FCSTD DOCUMENT  (FreeCAD 0.21R33771 (Git))
Label: Assemblage
License: All rights reserved
LicenseURL: http://en.wikipedia.org/wiki/All_rights_reserved
objects: App::DocumentObjectGroup×3, App::Link×2, PartDesign::CoordinateSystem×1, App::FeaturePython×1, App::Part×1
note: 1 computed .brp shape members not serialized (recipe doc carries the construction recipe); baked Part::Feature solids carry a one-line shape summary decoded from their .brp
EXTERNAL_REF file=Module HY-SRF05.FCStd obj=HY_SRF05
EXTERNAL_REF file=support_ultrasons-v3.FCStd obj=Body

FEATURE [App::DocumentObjectGroup] Parts
FEATURE [PartDesign::CoordinateSystem] LCS_Origin
  AttacherType = Attacher::AttachEngine3D
  MapMode = 2
  Support = -> [X_Axis]
FEATURE [App::DocumentObjectGroup] Constraints
FEATURE [App::FeaturePython] Variables  # WARN: FeaturePython — macro-defined, semantics opaque (R4)
  Type = App::PropertyContainer
FEATURE [App::DocumentObjectGroup] Configurations
FEATURE [App::Link] HY_SRF012  label="HY-SRF012"
  LinkPlacement = pos=(-0.75,-17,30.75) rot=(0,0.707107,-0.707107;3.14159rad)
  LinkedObject = -> <external Module HY-SRF05.FCStd>#HY_SRF05
  Placement = pos=(-0.75,-17,30.75) rot=(0,0.707107,-0.707107;3.14159rad)
FEATURE [App::Link] support_ultrasons  label="support-ultrasons"
  LinkedObject = -> <external support_ultrasons-v3.FCStd>#Body
FEATURE [App::Part] Assembly  label="Ensemble-US"
  AssemblyType = Part::Link
  Group = -> [LCS_Origin,Constraints,Variables,Configurations,HY_SRF012,support_ultrasons]
  Origin = -> Origin
  Type = Assembly

RESOLVED EXTERNAL PARTS (link-assembly join: the EXTERNAL_REF files above that resolve inside this repo's crawl, each included once):
---- part support_ultrasons-v3.FCStd = doc fcstd_a76cce11500f ----
FCSTD DOCUMENT  (FreeCAD 0.21R33771 (Git))
Label: support_ultrasons-v3
License: All rights reserved
LicenseURL: http://en.wikipedia.org/wiki/All_rights_reserved
objects: Sketcher::SketchObject×11, PartDesign::Pad×6, PartDesign::Pocket×5, PartDesign::Chamfer×2, PartDesign::Fillet×2, PartDesign::Body×1
note: 42 computed .brp shape members not serialized (recipe doc carries the construction recipe); baked Part::Feature solids carry a one-line shape summary decoded from their .brp

FEATURE [Sketcher::SketchObject] Sketch
  FullyConstrained = true
  MapMode = 5
  Support = -> [XY_Plane]
  sketch-geometry (6):
    g0: LineSegment StartX=-17.5 StartY=-15 StartZ=0 EndX=17.5 EndY=-15 EndZ=0
    g1: LineSegment StartX=17.5 StartY=-15 StartZ=0 EndX=17.5 EndY=-7 EndZ=0
    g2: LineSegment StartX=17.5 StartY=-7 StartZ=0 EndX=11 EndY=7 EndZ=0
    g3: LineSegment StartX=11 StartY=7 StartZ=0 EndX=-11 EndY=7 EndZ=0
    g4: LineSegment StartX=-17.5 StartY=-7 StartZ=0 EndX=-17.5 EndY=-15 EndZ=0
    g5: LineSegment StartX=-11 StartY=7 StartZ=0 EndX=-17.5 EndY=-7 EndZ=0
  constraints (18):
    c: Horizontal(g0)
    c: Coincident(g1,g0)
    c: Vertical(g1)
    c: Coincident(g2,g1)
    c: Coincident(g3,g2)
    c: Horizontal(g3)
    c: Coincident(g4,g0)
    c: Vertical(g4)
    c: Coincident(g5,g3)
    c: Coincident(g5,g4)
    c: DistanceY(g0,g2) = 22
    c: DistanceX(g3,g3) = 22
    c: DistanceX(g0,g0) = 35
    c: Equal(g2,g5)
    c: Equal(g1,g4)
    c: DistanceY(g1,g1) = 8
    c: DistanceX(g-1,g0) = 17.5
    c: DistanceY(g0,g-1) = 15
FEATURE [PartDesign::Pad] Pad
  Direction = (0,0,1)
  Length = 2
  Length2 = 10
  Profile = -> Sketch
  ReferenceAxis = -> Sketch [N_Axis]
  Type = 0
FEATURE [Sketcher::SketchObject] Sketch001
  ExternalGeometry = -> [Pad]
  FullyConstrained = true
  MapMode = 5
  Placement = pos=(0,0,2) rot=(0,0,1;0rad)
  Support = -> [Pad]
  sketch-geometry (4):
    g0: LineSegment StartX=-17.5 StartY=-15 StartZ=0 EndX=17.5 EndY=-15 EndZ=0
    g1: LineSegment StartX=17.5 StartY=-15 StartZ=0 EndX=17.5 EndY=-13 EndZ=0
    g2: LineSegment StartX=17.5 StartY=-13 StartZ=0 EndX=-17.5 EndY=-13 EndZ=0
    g3: LineSegment StartX=-17.5 StartY=-13 StartZ=0 EndX=-17.5 EndY=-15 EndZ=0
  constraints (11):
    c: Coincident(g0,g1)
    c: Coincident(g1,g2)
    c: Coincident(g2,g3)
    c: Coincident(g3,g0)
    c: Horizontal(g0)
    c: Horizontal(g2)
    c: Vertical(g1)
    c: Vertical(g3)
    c: Coincident(g0,g-3)
    c: DistanceY(g1,g1) = 2
    c: DistanceX(g2,g2) = 35
FEATURE [PartDesign::Pad] Pad001
  BaseFeature = -> Pad
  Direction = (0,0,1)
  Length = 18
  Length2 = 10
  Profile = -> Sketch001
  ReferenceAxis = -> Sketch001 [N_Axis]
  Type = 0
FEATURE [Sketcher::SketchObject] Sketch002
  ExternalGeometry = -> [Pad001]
  FullyConstrained = false
  MapMode = 5
  Placement = pos=(0,0,20) rot=(0,0,1;0rad)
  Support = -> [Pad001]
  sketch-geometry (7):
    g0: LineSegment StartX=-22 StartY=-13 StartZ=0 EndX=22 EndY=-13 EndZ=0
    g1: LineSegment StartX=22 StartY=-13 StartZ=0 EndX=22 EndY=-15 EndZ=0
    g2: LineSegment StartX=22 StartY=-15 StartZ=0 EndX=-22 EndY=-15 EndZ=0
    g3: LineSegment StartX=-22 StartY=-15 StartZ=0 EndX=-22 EndY=-13 EndZ=0
    g4: LineSegment StartX=-22 StartY=-13 StartZ=0 EndX=-17.5 EndY=-13 EndZ=0
    g5: LineSegment StartX=-22 StartY=-13 StartZ=0 EndX=-17.5 EndY=-15 EndZ=0
    g6: LineSegment StartX=22 StartY=-13 StartZ=0 EndX=17.5 EndY=-15 EndZ=0
  constraints (17):
    c: Coincident(g0,g1)
    c: Coincident(g1,g2)
    c: Coincident(g2,g3)
    c: Coincident(g3,g0)
    c: Horizontal(g0)
    c: Horizontal(g2)
    c: Vertical(g1)
    c: Vertical(g3)
    c: PointOnObject(g-4,g2)
    c: PointOnObject(g-3,g0)
    c: DistanceX(g2,g2) = 44
    c: Coincident(g4,g0)
    c: Coincident(g5,g0)
    c: Coincident(g5,g-4)
    c: Coincident(g6,g0)
    c: Coincident(g6,g-4)
    c: Equal(g6,g5)
FEATURE [PartDesign::Pad] Pad002
  BaseFeature = -> Pad001
  Direction = (0,0,1)
  Length = 24
  Length2 = 10
  Profile = -> Sketch002
  ReferenceAxis = -> Sketch002 [N_Axis]
  Type = 0
FEATURE [PartDesign::Chamfer] Chamfer
  Angle = 45
  Base = -> Pad002 [Edge13,Edge19]
  BaseFeature = -> Pad002
  ChamferType = 1
  FlipDirection = false
  Size = 4.49
  Size2 = 17.99
  SupportTransform = false
  UseAllEdges = false
FEATURE [PartDesign::Fillet] Fillet
  Base = -> Chamfer [Edge19,Edge43,Edge50,Edge48,Edge45,Edge18]
  BaseFeature = -> Chamfer
  Radius = 3
  SupportTransform = false
  UseAllEdges = false
FEATURE [Sketcher::SketchObject] Sketch003
  ExternalGeometry = -> [Fillet]
  FullyConstrained = true
  MapMode = 5
  Placement = pos=(0,-13,0) rot=(0,0.707107,0.707107;3.14159rad)
  Support = -> [Fillet]
  expr: Constraints[5] = .Constraints.largeur / 2
  sketch-geometry (2):
    g0: Circle CenterX=-19.05 CenterY=39 CenterZ=0 NormalX=0 NormalY=0 NormalZ=1 AngleXU=0 Radius=1
    g1: Circle CenterX=19.05 CenterY=24.014 CenterZ=0 NormalX=0 NormalY=0 NormalZ=1 AngleXU=0 Radius=1
  constraints (6):
    c: Equal(g1,g0)
    c: DistanceX(g0,g1) = 38.1  'largeur'
    c: DistanceY(g1,g0) = 14.986
    c: Diameter(g1) = 2  'percage'
    c: DistanceY(g-1,g0) = 39
    c: DistanceX(g-1,g1) = 19.05
FEATURE [PartDesign::Pocket] Pocket
  BaseFeature = -> Fillet
  Direction = (0,-1,2e-16)
  Length = 5
  Length2 = 5
  Profile = -> Sketch003
  ReferenceAxis = -> Sketch003 [N_Axis]
  Type = 0
FEATURE [Sketcher::SketchObject] Sketch004
  ExternalGeometry = -> [Pocket]
  FullyConstrained = true
  MapMode = 5
  Placement = pos=(0,0,2) rot=(0,0,1;0rad)
  Support = -> [Pocket]
  sketch-geometry (1):
    g0: Circle CenterX=0 CenterY=0 CenterZ=0 NormalX=0 NormalY=0 NormalZ=1 AngleXU=0 Radius=1.6
  constraints (2):
    c: Coincident(g0,g-1)
    c: Diameter(g0) = 3.2
FEATURE [PartDesign::Pocket] Pocket001
  BaseFeature = -> Pocket
  Direction = (0,0,-1)
  Length = 5
  Length2 = 5
  Profile = -> Sketch004
  ReferenceAxis = -> Sketch004 [N_Axis]
  Type = 0
FEATURE [Sketcher::SketchObject] Sketch005
  ExternalGeometry = -> [Pocket001]
  FullyConstrained = true
  MapMode = 5
  Placement = pos=(0,0,2) rot=(0,0,1;0rad)
  Support = -> [Pocket001]
  sketch-geometry (8):
    g0: LineSegment StartX=-9.5 StartY=-13 StartZ=0 EndX=-8 EndY=-13 EndZ=0
    g1: LineSegment StartX=-8 StartY=-13 StartZ=0 EndX=-8 EndY=1 EndZ=0
    g2: LineSegment StartX=-8 StartY=1 StartZ=0 EndX=-9.5 EndY=1 EndZ=0
    g3: LineSegment StartX=-9.5 StartY=1 StartZ=0 EndX=-9.5 EndY=-13 EndZ=0
    g4: LineSegment StartX=8 StartY=-13 StartZ=0 EndX=9.5 EndY=-13 EndZ=0
    g5: LineSegment StartX=9.5 StartY=-13 StartZ=0 EndX=9.5 EndY=1 EndZ=0
    g6: LineSegment StartX=9.5 StartY=1 StartZ=0 EndX=8 EndY=1 EndZ=0
    g7: LineSegment StartX=8 StartY=1 StartZ=0 EndX=8 EndY=-13 EndZ=0
  constraints (23):
    c: Coincident(g0,g1)
    c: Coincident(g1,g2)
    c: Coincident(g2,g3)
    c: Coincident(g3,g0)
    c: Horizontal(g0)
    c: Horizontal(g2)
    c: Vertical(g1)
    c: Vertical(g3)
    c: PointOnObject(g0,g-3)
    c: Coincident(g4,g5)
    c: Coincident(g5,g6)
    c: Coincident(g6,g7)
    c: Coincident(g7,g4)
    c: Horizontal(g4)
    c: Horizontal(g6)
    c: Vertical(g5)
    c: Vertical(g7)
    c: PointOnObject(g4,g-3)
    c: Symmetric(g6,g1,g-2)
    c: Equal(g6,g2)
    c: DistanceX(g-1,g6) = 8
    c: DistanceX(g6,g6) = 1.5
    c: DistanceY(g5,g5) = 14
FEATURE [PartDesign::Pad] Pad003
  BaseFeature = -> Pocket001
  Direction = (0,0,1)
  Length = 35
  Length2 = 10
  Profile = -> Sketch005
  ReferenceAxis = -> Sketch005 [N_Axis]
  Type = 0
FEATURE [PartDesign::Chamfer] Chamfer001
  Angle = 45
  Base = -> Pad003 [Edge34,Edge44]
  BaseFeature = -> Pad003
  ChamferType = 1
  FlipDirection = false
  Size = 10
  Size2 = 30
  SupportTransform = false
  UseAllEdges = false
FEATURE [PartDesign::Fillet] Fillet001
  Base = -> Chamfer001 [Edge94,Edge11,Edge8,Edge76]
  BaseFeature = -> Chamfer001
  Radius = 3
  SupportTransform = false
  UseAllEdges = false
FEATURE [Sketcher::SketchObject] Sketch006
  ExternalGeometry = -> [Fillet001]
  FullyConstrained = true
  MapMode = 5
  Placement = pos=(0,-13,0) rot=(0,0.707107,0.707107;3.14159rad)
  Support = -> [Fillet001]
  sketch-geometry (4):
    g0: LineSegment StartX=-7.75 StartY=2 StartZ=0 EndX=-7.75 EndY=24 EndZ=0
    g1: LineSegment StartX=7.75 StartY=2 StartZ=0 EndX=7.75 EndY=24 EndZ=0
    g2: ArcOfCircle CenterX=1e-16 CenterY=24 CenterZ=0 NormalX=0 NormalY=0 NormalZ=1 AngleXU=0 Radius=7.75 StartAngle=0 EndAngle=3.14159
    g3: LineSegment StartX=-7.75 StartY=2 StartZ=0 EndX=7.75 EndY=2 EndZ=0
  constraints (12):
    c: PointOnObject(g0,g-3)
    c: Vertical(g0)
    c: PointOnObject(g1,g-3)
    c: Vertical(g1)
    c: Symmetric(g1,g0,g-2)
    c: DistanceY(g1,g1) = 22
    c: Coincident(g2,g0)
    c: Coincident(g2,g1)
    c: Horizontal(g2,g1)
    c: Coincident(g3,g0)
    c: Coincident(g3,g1)
    c: DistanceX(g0,g1) = 15.5
FEATURE [PartDesign::Pocket] Pocket002
  BaseFeature = -> Fillet001
  Direction = (0,-1,2e-16)
  Length = 5
  Length2 = 5
  Profile = -> Sketch006
  ReferenceAxis = -> Sketch006 [N_Axis]
  Type = 0
FEATURE [Sketcher::SketchObject] Sketch007
  ExternalGeometry = -> [Pocket002]
  FullyConstrained = true
  MapMode = 5
  Placement = pos=(0,-15,0) rot=(1,0,0;1.5708rad)
  Support = -> [Pocket002]
  sketch-geometry (2):
    g0: Circle CenterX=-19.05 CenterY=24.014 CenterZ=0 NormalX=0 NormalY=0 NormalZ=1 AngleXU=0 Radius=2.3
    g1: Circle CenterX=19.05 CenterY=39 CenterZ=0 NormalX=0 NormalY=0 NormalZ=1 AngleXU=0 Radius=2.3
  constraints (4):
    c: Coincident(g0,g-4)
    c: Coincident(g1,g-3)
    c: Equal(g1,g0)
    c: Diameter(g1) = 4.6  'Entretoise'
FEATURE [PartDesign::Pad] Pad004
  BaseFeature = -> Pocket002
  Direction = (0,-1,2e-16)
  Length = 2
  Length2 = 10
  Profile = -> Sketch007
  ReferenceAxis = -> Sketch007 [N_Axis]
  Type = 0
FEATURE [Sketcher::SketchObject] Sketch008
  ExternalGeometry = -> [Pad004]
  FullyConstrained = true
  MapMode = 5
  Placement = pos=(1.4e-15,-17,5e-16) rot=(1,0,0;1.5708rad)
  Support = -> [Pad004]
  sketch-geometry (2):
    g0: Circle CenterX=19.05 CenterY=39 CenterZ=0 NormalX=0 NormalY=0 NormalZ=1 AngleXU=0 Radius=1
    g1: Circle CenterX=-19.05 CenterY=24.014 CenterZ=0 NormalX=0 NormalY=0 NormalZ=1 AngleXU=0 Radius=1
  constraints (4):
    c: Coincident(g0,g-3)
    c: Coincident(g1,g-4)
    c: Equal(g0,g1)
    c: Diameter(g0) = 2  'Entretoise'
FEATURE [PartDesign::Pocket] Pocket003
  BaseFeature = -> Pad004
  Direction = (-1e-16,1,-2e-16)
  Length = 5
  Length2 = 5
  Profile = -> Sketch008
  ReferenceAxis = -> Sketch008 [N_Axis]
  Type = 1
FEATURE [Sketcher::SketchObject] Sketch009
  ExternalGeometry = -> [Pocket003]
  FullyConstrained = true
  MapMode = 5
  Placement = pos=(0,-13,0) rot=(0,0.707107,0.707107;3.14159rad)
  Support = -> [Pocket003]
  expr: Constraints[3] = <<Sketch007>>.Constraints.Entretoise
  sketch-geometry (2):
    g0: Circle CenterX=-19.05 CenterY=39 CenterZ=0 NormalX=0 NormalY=0 NormalZ=1 AngleXU=0 Radius=2.3
    g1: Circle CenterX=19.05 CenterY=24.014 CenterZ=0 NormalX=0 NormalY=0 NormalZ=1 AngleXU=0 Radius=2.3
  constraints (4):
    c: Coincident(g0,g-6)
    c: Coincident(g1,g-4)
    c: Equal(g1,g0)
    c: Diameter(g1) = 4.6
FEATURE [PartDesign::Pad] Pad005
  BaseFeature = -> Pocket003
  Direction = (0,1,-2e-16)
  Length = 2.5
  Length2 = 10
  Profile = -> Sketch009
  ReferenceAxis = -> Sketch009 [N_Axis]
  Type = 0
FEATURE [Sketcher::SketchObject] Sketch010
  ExternalGeometry = -> [Pad005]
  FullyConstrained = true
  MapMode = 5
  Placement = pos=(8e-16,-10.5,3e-16) rot=(0,0.707107,0.707107;3.14159rad)
  Support = -> [Pad005]
  expr: Constraints[3] = <<Sketch003>>.Constraints.percage
  sketch-geometry (2):
    g0: Circle CenterX=-19.05 CenterY=39 CenterZ=0 NormalX=0 NormalY=0 NormalZ=1 AngleXU=0 Radius=1
    g1: Circle CenterX=19.05 CenterY=24.014 CenterZ=0 NormalX=0 NormalY=0 NormalZ=1 AngleXU=0 Radius=1
  constraints (4):
    c: Coincident(g0,g-3)
    c: Coincident(g1,g-4)
    c: Equal(g1,g0)
    c: Diameter(g1) = 2
FEATURE [PartDesign::Pocket] Pocket004
  BaseFeature = -> Pad005
  Direction = (1e-16,-1,2e-16)
  Length = 5
  Length2 = 5
  Profile = -> Sketch010
  ReferenceAxis = -> Sketch010 [N_Axis]
  Type = 0
FEATURE [PartDesign::Body] Body  label="support-ultrasons"
  Group = -> [Sketch,Pad,Sketch001,Pad001,Sketch002,Pad002,Chamfer,Fillet,Sketch003,Pocket,Sketch004,Pocket001,Sketch005,Pad003,Chamfer001,Fillet001,Sketch006,Pocket002,Sketch007,Pad004,Sketch008,Pocket003,Sketch009,Pad005,Sketch010,Pocket004]
  Origin = -> Origin
  Tip = -> Pocket004
